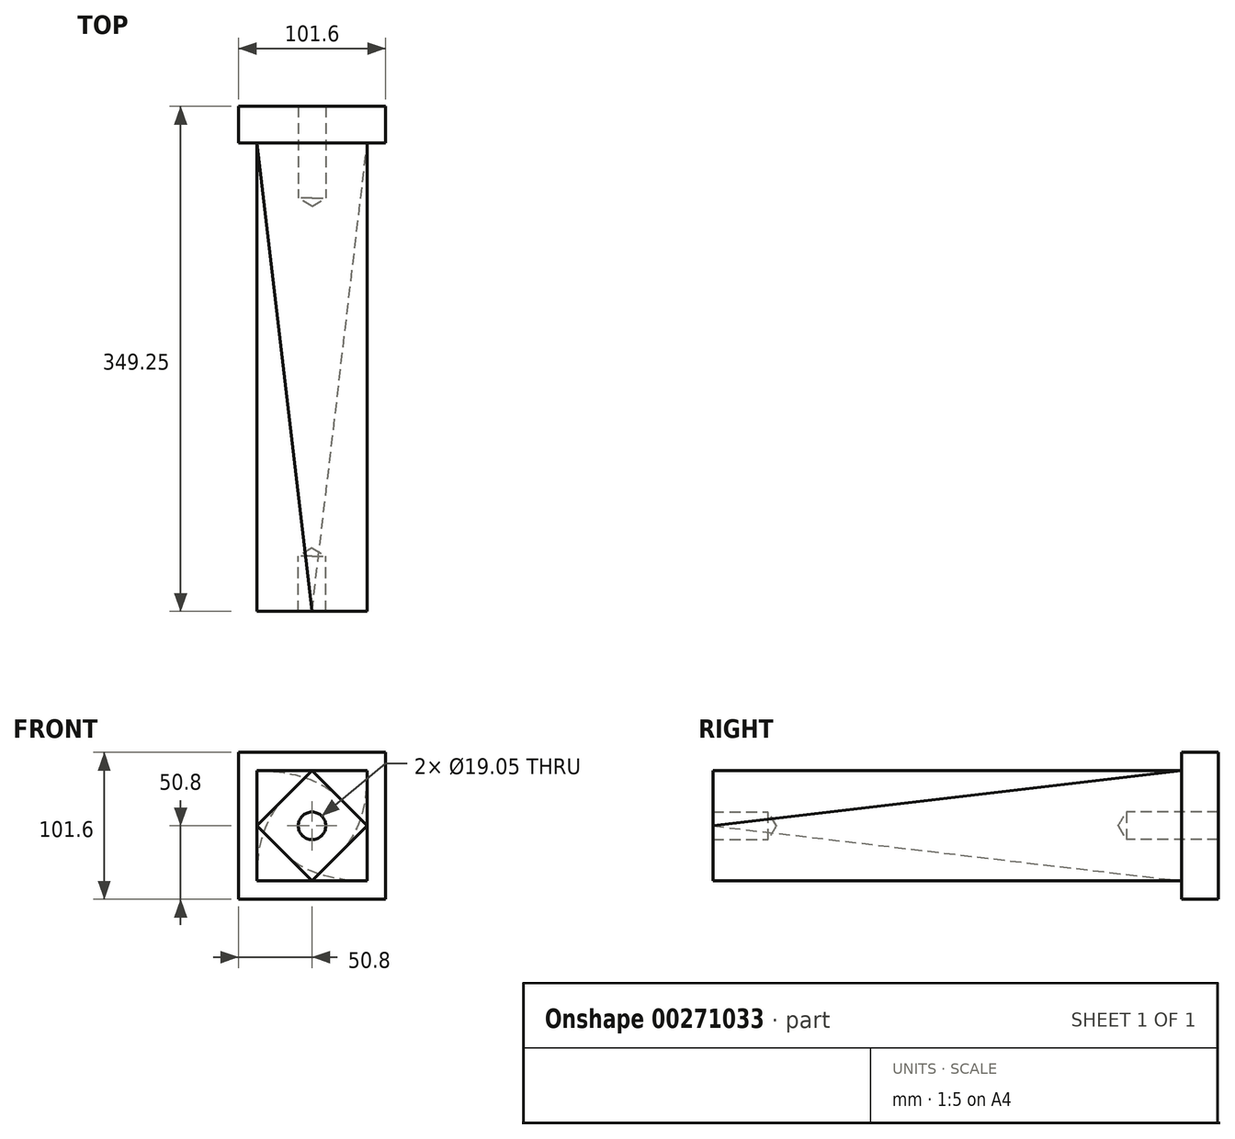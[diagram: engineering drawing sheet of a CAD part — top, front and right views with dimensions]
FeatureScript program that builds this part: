
annotation { "Feature Type Name" : "Feature", "Feature Type Description" : "" }
export const myFeature = defineFeature(function(context is Context, id is Id, definition is map)
    precondition{}
    {
        {
            var Q0;
            Q0=qCreatedBy(makeId("Front.planeOp"),FACE);
            var sketch = newSketch(context, id + "F0", { "sketchPlane" : qUnion([Q0])});
            skLineSegment(sketch, "E0.bottom", {"start": v(0, 0) * mm, "end": v(101.6, 0) * mm});
            skLineSegment(sketch, "E0.top", {"start": v(0, 101.6) * mm, "end": v(101.6, 101.6) * mm});
            skLineSegment(sketch, "E0.left", {"start": v(0, 0) * mm, "end": v(0, 101.6) * mm});
            skLineSegment(sketch, "E0.right", {"start": v(101.6, 0) * mm, "end": v(101.6, 101.6) * mm});
            skSolve(sketch);
        }
        {
            var Q0;
            Q0 = qSketchRegion(id + "F0", true);
            extrude(context, id + "F1", {"entities" : qUnion([Q0]), "depth" : 25.4 * mm});
        }
        {
            var Q0;
            Q0=makeQuery(id+"F1.opExtrude","CAP_FACE",FACE,{"disambiguationData":[OSD([sQuery(id+"F0.wireOp",EDGE,"E0.bottom"),sQuery(id+"F0.wireOp",EDGE,"E0.top"),sQuery(id+"F0.wireOp",EDGE,"E0.left"),sQuery(id+"F0.wireOp",EDGE,"E0.right")])],"isStart":false});
            cPlane(context, id + "F2", {"entities" : qUnion([Q0]), "cplaneType" : CPlaneType.OFFSET, "offset" : 323.85 * mm, "width" : 152.4 * mm, "height" : 152.4 * mm});
        }
        {
            var Q0;
            Q0=qCreatedBy(id+"F2.planeOp",FACE);
            var sketch = newSketch(context, id + "F3", { "sketchPlane" : qUnion([Q0])});
            skLineSegment(sketch, "E1", {"start": v(50.8, 88.9) * mm, "end": v(12.7, 50.8) * mm});
            skPoint(sketch, "E1.startSnap0", {"position": v(50.8, 101.6) * mm});
            skPoint(sketch, "E1.endSnap0", {"position": v(0, 50.8) * mm});
            skLineSegment(sketch, "E2", {"start": v(12.7, 50.8) * mm, "end": v(50.8, 12.7) * mm});
            skPoint(sketch, "E2.endSnap0", {"position": v(50.8, 0) * mm});
            skLineSegment(sketch, "E3", {"start": v(50.8, 12.7) * mm, "end": v(88.9, 50.8) * mm});
            skPoint(sketch, "E3.endSnap0", {"position": v(101.6, 50.8) * mm});
            skLineSegment(sketch, "E4", {"start": v(88.9, 50.8) * mm, "end": v(50.8, 88.9) * mm});
            skSolve(sketch);
        }
        {
            var Q0;
            Q0=makeQuery(id+"F1.opExtrude","CAP_FACE",FACE,{"disambiguationData":[OSD([sQuery(id+"F0.wireOp",EDGE,"E0.bottom"),sQuery(id+"F0.wireOp",EDGE,"E0.top"),sQuery(id+"F0.wireOp",EDGE,"E0.left"),sQuery(id+"F0.wireOp",EDGE,"E0.right")])],"isStart":false});
            var sketch = newSketch(context, id + "F4", { "sketchPlane" : qUnion([Q0])});
            skLineSegment(sketch, "E5.bottom", {"start": v(12.7, 12.7) * mm, "end": v(88.9, 12.7) * mm});
            skLineSegment(sketch, "E5.top", {"start": v(12.7, 88.9) * mm, "end": v(88.9, 88.9) * mm});
            skLineSegment(sketch, "E5.left", {"start": v(12.7, 12.7) * mm, "end": v(12.7, 88.9) * mm});
            skLineSegment(sketch, "E5.right", {"start": v(88.9, 12.7) * mm, "end": v(88.9, 88.9) * mm});
            skSolve(sketch);
        }
        {
            var Q1;
            Q1=makeQuery(id+"F3.imprint","IMPRINT",FACE,{"disambiguationData":[TD([[makeQuery(id+"F3.imprint","IMPRINT",EDGE,{"derivedFrom":sQuery(id+"F3.wireOp",EDGE,"E1")}),1.0]])]});
            var Q2;
            Q2=makeQuery(id+"F4.imprint","IMPRINT",FACE,{"disambiguationData":[TD([[makeQuery(id+"F4.imprint","IMPRINT",EDGE,{"derivedFrom":sQuery(id+"F4.wireOp",EDGE,"E5.bottom")}),1.0]])]});
            loft(context, id + "F5", {"operationType" : NewBodyOperationType.ADD, "sheetProfilesArray" : [{ "sheetProfileEntities" : qUnion([Q1]) }, { "sheetProfileEntities" : qUnion([Q2]) }]});
        }
        {
            var Q0;
            Q0=makeQuery(id+"F1.opExtrude","CAP_FACE",FACE,{"disambiguationData":[OSD([sQuery(id+"F0.wireOp",EDGE,"E0.bottom"),sQuery(id+"F0.wireOp",EDGE,"E0.top"),sQuery(id+"F0.wireOp",EDGE,"E0.left"),sQuery(id+"F0.wireOp",EDGE,"E0.right")])],"isStart":true});
            var sketch = newSketch(context, id + "F6", { "sketchPlane" : qUnion([Q0])});
            skPoint(sketch, "E6", {"position": v(-50.8, 50.8) * mm});
            skPoint(sketch, "E6.positionSnap0", {"position": v(-50.8, 101.6) * mm});
            skPoint(sketch, "E6.positionSnap1", {"position": v(-101.6, 50.8) * mm});
            skSolve(sketch);
        }
        {
            var Q0;
            Q0=sQuery(id+"F6.wireOp",VERTEX,"E6");
            var Q1;
            Q1=makeQuery(id+"F1.opExtrude","SWEPT_BODY",BODY,{"disambiguationData":[OSD([sQuery(id+"F0.wireOp",EDGE,"E0.bottom"),sQuery(id+"F0.wireOp",EDGE,"E0.top"),sQuery(id+"F0.wireOp",EDGE,"E0.left"),sQuery(id+"F0.wireOp",EDGE,"E0.right")])]});
            hole(context, id + "F7", {"style" : HoleStyle.SIMPLE, "endStyle" : HoleEndStyle.BLIND, "holeDiameter" : 19.05 * mm, "holeDepth" : 63.5 * mm, "tappedDepth" : 12.7 * mm, "tapClearance" : 3, "locations" : qUnion([Q0]), "scope" : qUnion([Q1])});
        }
        {
            var Q0;
            Q0=makeQuery(id+"F5.opLoft","CAP_FACE",FACE,{"disambiguationData":[OSD([makeQuery(id+"F3.imprint","IMPRINT",FACE,{"disambiguationData":[TD([[makeQuery(id+"F3.imprint","IMPRINT",EDGE,{"derivedFrom":sQuery(id+"F3.wireOp",EDGE,"E1")}),1.0]])]})])],"isStart":true});
            var sketch = newSketch(context, id + "F8", { "sketchPlane" : qUnion([Q0])});
            skPoint(sketch, "E7", {"position": v(50.8, 50.8) * mm});
            skSolve(sketch);
        }
        {
            var Q0;
            Q0=sQuery(id+"F8.wireOp",VERTEX,"E7");
            var Q1;
            Q1=makeQuery(id+"F1.opExtrude","SWEPT_BODY",BODY,{"disambiguationData":[OSD([sQuery(id+"F0.wireOp",EDGE,"E0.bottom"),sQuery(id+"F0.wireOp",EDGE,"E0.top"),sQuery(id+"F0.wireOp",EDGE,"E0.left"),sQuery(id+"F0.wireOp",EDGE,"E0.right")])]});
            hole(context, id + "F9", {"style" : HoleStyle.SIMPLE, "endStyle" : HoleEndStyle.BLIND, "holeDiameter" : 19.05 * mm, "holeDepth" : 38.1 * mm, "tappedDepth" : 12.7 * mm, "tapClearance" : 3, "locations" : qUnion([Q0]), "scope" : qUnion([Q1])});
        }
    });
